# Revit family: Grohe_BathMixer_25248KF1
name_source: partatom
category: Plumbing Fixtures
units: mm (PartAtom-declared; Revit-internal decimal feet)

## family parameters
Cut with Voids When Loaded = No
Host = Face
OmniClass Number = 23.45.05.00
OmniClass Title = Sanitary Equipment
Part Type = Normal
Room Calculation Point = No
Round Connector Dimension = Use Diameter
Shared = No

## types (1)
- Bath Mixer (25248KF1)
    Assembly Code = D2013
    AssetType = Fixed
    BIMObjectName = Grohe_BathMixer_25248KF1
    CO2NeutralProduction = GROHE is one of the first leading manufacturer within the sanitary industry having a CO2-neutral production.
    ClassificationName = Uniclass2015
    ClassificationValue = Pr_40_20_87_55
    Color = Grohe_Black
    Cost = 0 $
    Default Elevation = 0 mm  [stored 0 ft]
    Description = Bath Mixer
    DimensionsDocumentLink = https://cdn.cloud.grohe.com
    DocumentationCertificates = https://www.bimstore.co
    DocumentationInstallationGuide = https://www.bimstore.co
    DocumentationLiterature = https://www.bimstore.co
    DocumentationMaintenance = https://www.bimstore.co
    DocumentationTechnical = https://www.bimstore.co
    DurationUnit = Years
    EF000003 = Floor
    EF000139 = Other
    EF002149 = TRUE
    EF002286 = Insert (push coupling)
    EF002671 = Black
    EF007955 = FALSE
    EF011775 = EB
    EF011779 = FALSE
    EF014578 = true
    EF014591 = false
    EF016731 = Group I,<= 20 dB(A)
    EF020105 = No
    EF020259 = Downwards
    EF020780 = Single-grip
    EF020781 = Plastic cartridge
    EF020785 = M26 x 1.5
    EF020787 = Group II, <=30 dB(A)
    EF020789 = 277
    EF020791 = Stainless steel
    EF020799 = TRUE
    EF020805 = false
    EF020967 = false
    EF021035 = false
    EF021808 = 1-hole
    EF021835 = 0
    EF021855 = true
    EF022042 = Z
    EF022337 = 1/2 inch- 3/4 inch
    EF023686 = Other
    EF023687 = FALSE
    EF023688 = Foam jet nozzle
    EF023957 = TRUE
    EF024919 = false
    EF025109 = Other
    EFDE0022 = None
    EFNL0001 = true
    EFSE0002 = true
    Ecojoy = No
    ExpectedLife = 0
    Finish = Black
    FullRecyclabilityOfPlastic = All plastic components are fully recycable
    GROHESocialCommittment = green.grohe.com/social_engagement
    GROHESustainability = green.grohe.com
    IfcExportAs = IfcPipeFitting
    IfcExportType = IfcPipeFittingType
    Keynote = N16
    Manufacturer = Grohe
    ManufacturerName = Grohe
    Model = Bath Mixer
    ModelNumber = 25248KF1
    ModelReference = Bath Mixer
    NBSDescription = Shower fittings package
    NBSObjectName = Grohe - Shower fittings package
    NBSReference = 45-35-70/292
    NominalDepth = 0 mm  [stored 0 ft]
    NominalHeight = 0 mm  [stored 0 ft]
    NominalLength = 0 mm  [stored 0 ft]
    PQDiagramLink = https://cdn.cloud.grohe.com
    PrimaryMaterial = Grohe_Black
    ProductDescription = set for final installation for

45 984

without roughing-in set

GROHE SilkMove 35 mm ceramic cartridge

with temperature limiter

GROHE Long-Life finish

automatic diverter: bath/shower

swivel spout with mousseur and stop limiter

projection 277 mm

integrated non-return valve in the shower outlet 1/2"

with shower holder

hand shower (26 465)

Silverflex shower hose 1250 mm 1/2" x 1/2" (28 362)

protected against backflow

min. recommended pressure 1.0 bar
    ProductNumber = 25248KF1
    ProductShortText = Single-lever bath mixer 1/2" floor mounted
    ProductType = Single Lever Mixer
    ProductionYear = 2023
    SustainabilityAward = green.grohe.com/awards
    SustainabilityReport = green.grohe.com/reporting
    TPIDocumentLink = https://cdn.cloud.grohe.com
    Type Comments = Bath Mixer
    TypeName = Bath Mixer
    URL = https://www.grohe.co.uk
    WarrantyDurationLabor = 0
    WarrantyDurationParts = 0
    WarrantyDurationUnit = Years
    _BSBibleVersion = 17
    _BimSpecGuid = 0
    _CurrentRevision = 1
    _DistributedBy = https://www.bimstore.co
    _ObjectUserGuide = https://www.bimstore.co

note: [stored X ft] marks values corroborated as IEEE doubles in the binary element streams (Revit-internal decimal feet)

## geometry (parser evidence)
native form markers: Sweep x1
no freeform markers — native parametric forms only
